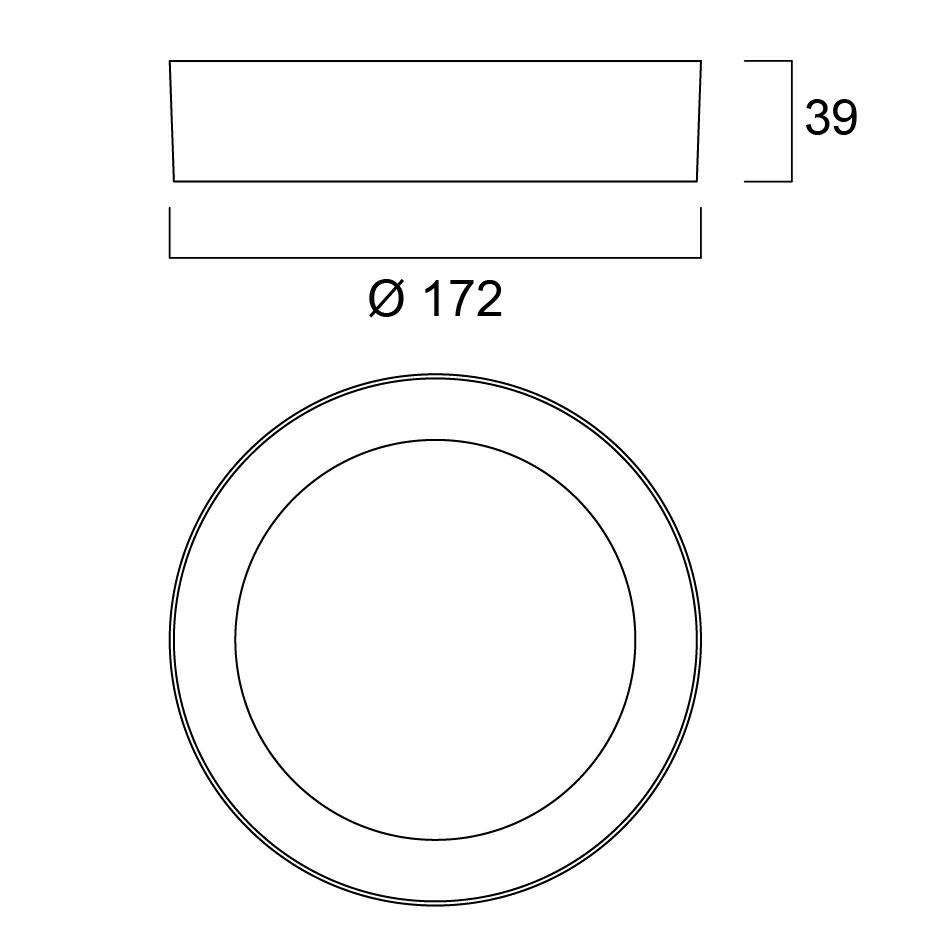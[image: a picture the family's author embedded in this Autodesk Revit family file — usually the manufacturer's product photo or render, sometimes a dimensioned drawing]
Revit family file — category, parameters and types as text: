
# Revit family: 0053902
name_source: partatom
category: Lighting Fixtures
revit_build: Autodesk Revit 2016 (Build: 20150220_1215(x64)
units: mm (PartAtom-declared; Revit-internal decimal feet)

## family parameters
Cut with Voids When Loaded = No
Host = Face
Light Source = Yes
OmniClass Number = 23.80.70.00
OmniClass Title = Lighting
Part Type = Normal
Room Calculation Point = No
Round Connector Dimension = Use Diameter
Shared = No

## types (1)
- 0053902 ST eco Downlight Flat 226 1925lm 830 DIM S
    Apparent Load = 20 VA
    Assembly Code = D5020200
    AssetType = Fixed
    ClassificationName = Uniclass2015
    ClassificationValue = EF_70_80
    Color Filter = 16777215
    Cost = 0 $
    Default Elevation = 1219 mm
    Description = Integrated LED surface mounted downlight providing 1940 fixture lumens at a wattage of 23W giving a high efficacy of 84lm/W. Fitting includes Leading/Trailing edge phase dimmable driver and has a round outer dimmension of of 226x226x39mm with an IP20 and IK02 rating providing uniform distribution with an Opal diffuser and 110° beam angle. Provided including a Loop in Loop out box and built with a white aluminium housing.
    Dimming Lamp Color Temperature Shift = <None>
    DimmingControlOptions = Dimmable
    DocumentationLiterature = http://www.sylvania-lighting.com
    DurationUnit = hours
    ElectricShockClassification = Class II
    Emit Shape Visible in Rendering = No
    Emit from Circle Diameter = 170 mm
    ExpectedLife = 50000
    IfcExportAs = IfcLightFixtureType
    IfcExportType = IfcLightFixtureType
    ImpactProtectionIndex = IK06
    IngressProtection = IP20
    InputNominalFrequency = 50/60 Hz
    InputVoltage = 220-240V~
    Keynote = 16500
    Lamp = LED
    LampColourRenderingIndex = 80
    LampColourTemperature = 3000 K
    LampNominalLuminous = 1925 lm
    LampsType = LED
    LuminousEfficacy = 96.25 lm/W
    Manufacturer = Feilo Sylvania
    ManufacturerName = Feilo Sylvania
    Material = aluminium housing, polystyrene diffuser
    Material_1_FEILO = Body-Sylvania-SylflatSurface-White
    Material_2_FEILO = LED-Sylvania-SylflatSurface
    Material_3_FEILO = <By Category>
    Material_4_FEILO = <By Category>
    Model = ST eco Downlight Flat 226 1925lm 830 DIM S
    ModelNumber = 0053902
    ModelReference = ST eco Downlight Flat 226 1925lm 830 DIM S
    Name = ST eco Downlight Flat 226 1925lm 830 DIM S
    NominalDepth = 226 mm  [stored 0.74147 ft]
    NominalHeight = 39 mm  [stored 0.127953 ft]
    NominalLength = 226 mm  [stored 0.74147 ft]
    Photometric Web File = 0053902.ies
    PowerConsumption = 20 W
    PowerFactor = 0.9
    RadiusDiffuser_FEILO = 7 mm  [stored 0.0229659 ft]
    RadiusSquare_FEILO = 10 mm  [stored 0.0328084 ft]
    Round_FEILO = Yes
    Square_FEILO = No
    Tilt Angle = -90.00°
    Type Image = <None>
    TypeName = ST eco Downlight Flat 226 1925lm 830 DIM S
    URL = http://www.sylvania-lighting.com
    Voltage = 230 V
    Weight = 6.54 kg
    WidthDiffuser_FEILO = 170 mm
    Width_FEILO = 226 mm  [stored 0.74147 ft]

note: [stored X ft] marks values corroborated as IEEE doubles in the binary element streams (Revit-internal decimal feet)

## geometry (parser evidence)
native form markers: Sweep x1
no freeform markers — native parametric forms only
